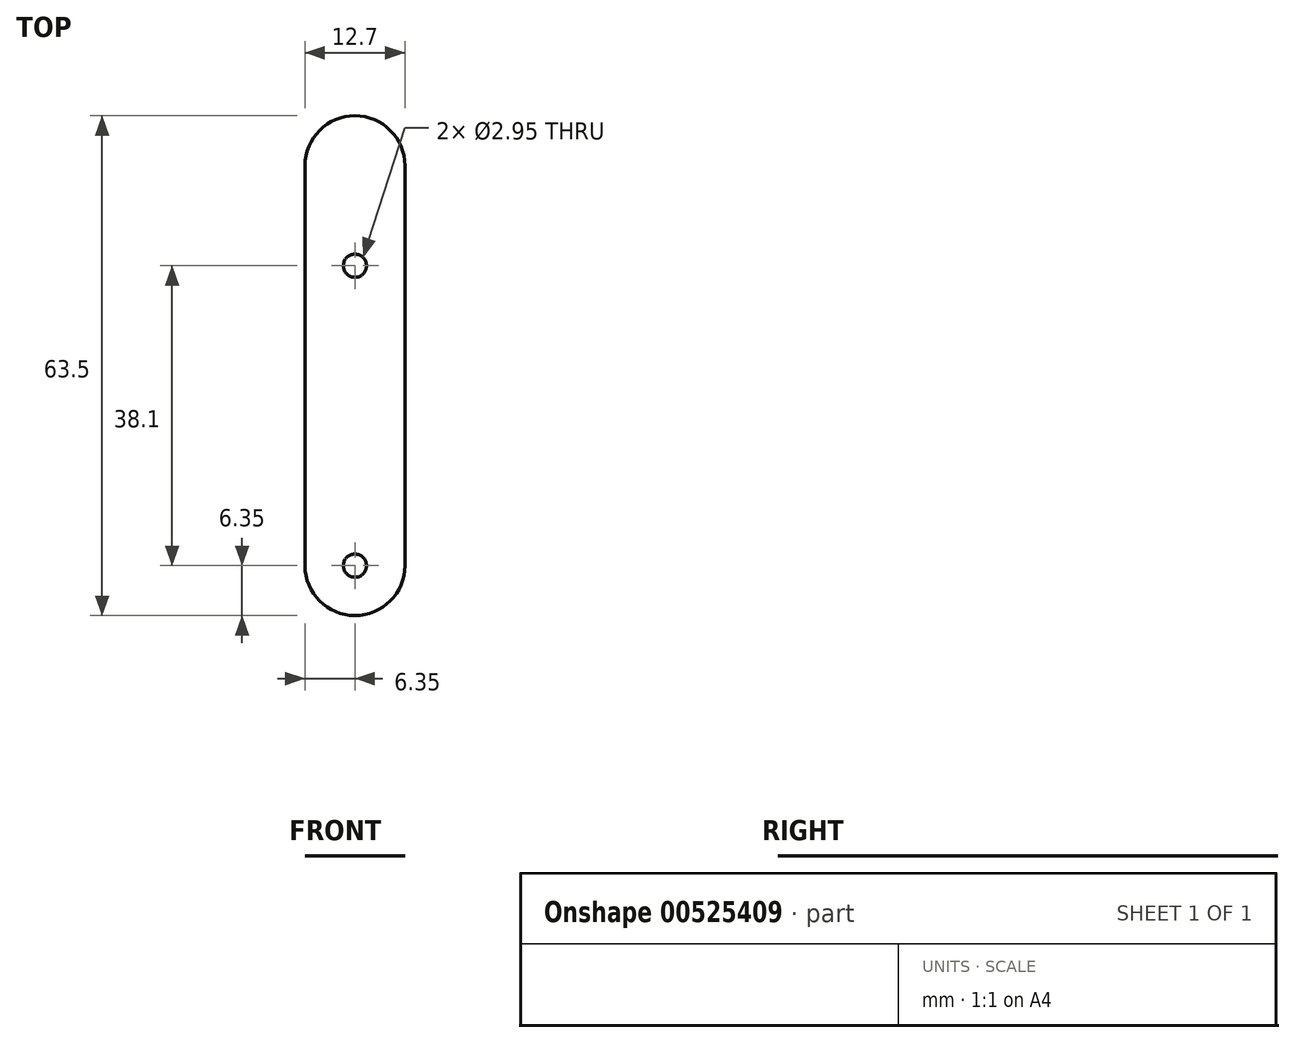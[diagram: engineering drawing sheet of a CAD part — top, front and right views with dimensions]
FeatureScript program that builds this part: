
annotation { "Feature Type Name" : "Feature", "Feature Type Description" : "" }
export const myFeature = defineFeature(function(context is Context, id is Id, definition is map)
    precondition{}
    {
        {
            var Q0;
            Q0=qCreatedBy(makeId("Top.planeOp"),FACE);
            var sketch = newSketch(context, id + "F0", { "sketchPlane" : qUnion([Q0])});
            skLineSegment(sketch, "E0.top", {"start": v(0, -25.4) * mm, "end": v(0, -25.4) * mm});
            skLineSegment(sketch, "E0.left", {"start": v(6.35, 25.4) * mm, "end": v(6.35, -19.05) * mm});
            skLineSegment(sketch, "E0.right", {"start": v(-6.35, 25.4) * mm, "end": v(-6.35, -19.05) * mm});
            skPoint(sketch, "E0.middle", {"position": v(0, 0) * mm});
            skCircle(sketch, "E1", {"center": v(0, -19.05) * mm, "radius": 1.47 * mm});
            skCircle(sketch, "E2.MirrorC", {"center": v(0, 19.05) * mm, "radius": 1.47 * mm});
            skLineSegment(sketch, "E3.top", {"start": v(0, 38.1) * mm, "end": v(0, 38.1) * mm});
            skLineSegment(sketch, "E3.left", {"start": v(-6.35, 25.4) * mm, "end": v(-6.35, 31.75) * mm});
            skLineSegment(sketch, "E3.right", {"start": v(6.35, 25.4) * mm, "end": v(6.35, 31.75) * mm});
            skPoint(sketch, "E4.visualSharp", {"position": v(-6.35, 38.1) * mm});
            skArc(sketch, "E4.filletArc", {"start": v(0, 38.1) * mm, "mid": v(-4.5, 36.24) * mm, "end": v(-6.35, 31.75) * mm});
            skPoint(sketch, "E5.visualSharp", {"position": v(6.35, 38.1) * mm});
            skArc(sketch, "E5.filletArc", {"start": v(6.35, 31.75) * mm, "mid": v(4.5, 36.24) * mm, "end": v(0, 38.1) * mm});
            skPoint(sketch, "E6.visualSharp", {"position": v(-6.35, -25.4) * mm});
            skArc(sketch, "E6.filletArc", {"start": v(-6.35, -19.05) * mm, "mid": v(-4.5, -23.54) * mm, "end": v(0, -25.4) * mm});
            skPoint(sketch, "E7.visualSharp", {"position": v(6.35, -25.4) * mm});
            skArc(sketch, "E7.filletArc", {"start": v(0, -25.4) * mm, "mid": v(4.5, -23.54) * mm, "end": v(6.35, -19.05) * mm});
            skSolve(sketch);
        }
        {
            var Q0;
            Q0=makeQuery(id+"F0.imprint","IMPRINT",FACE,{"disambiguationData":[TD([[makeQuery(id+"F0.imprint","IMPRINT",EDGE,{"derivedFrom":sQuery(id+"F0.wireOp",EDGE,"E0.left")}),-1.0]])]});
            extrude(context, id + "F1", {"entities" : qUnion([Q0]), "depth" : 1 / 203.2 * mm, "offsetDistance" : 25.4 * mm});
        }
    });
